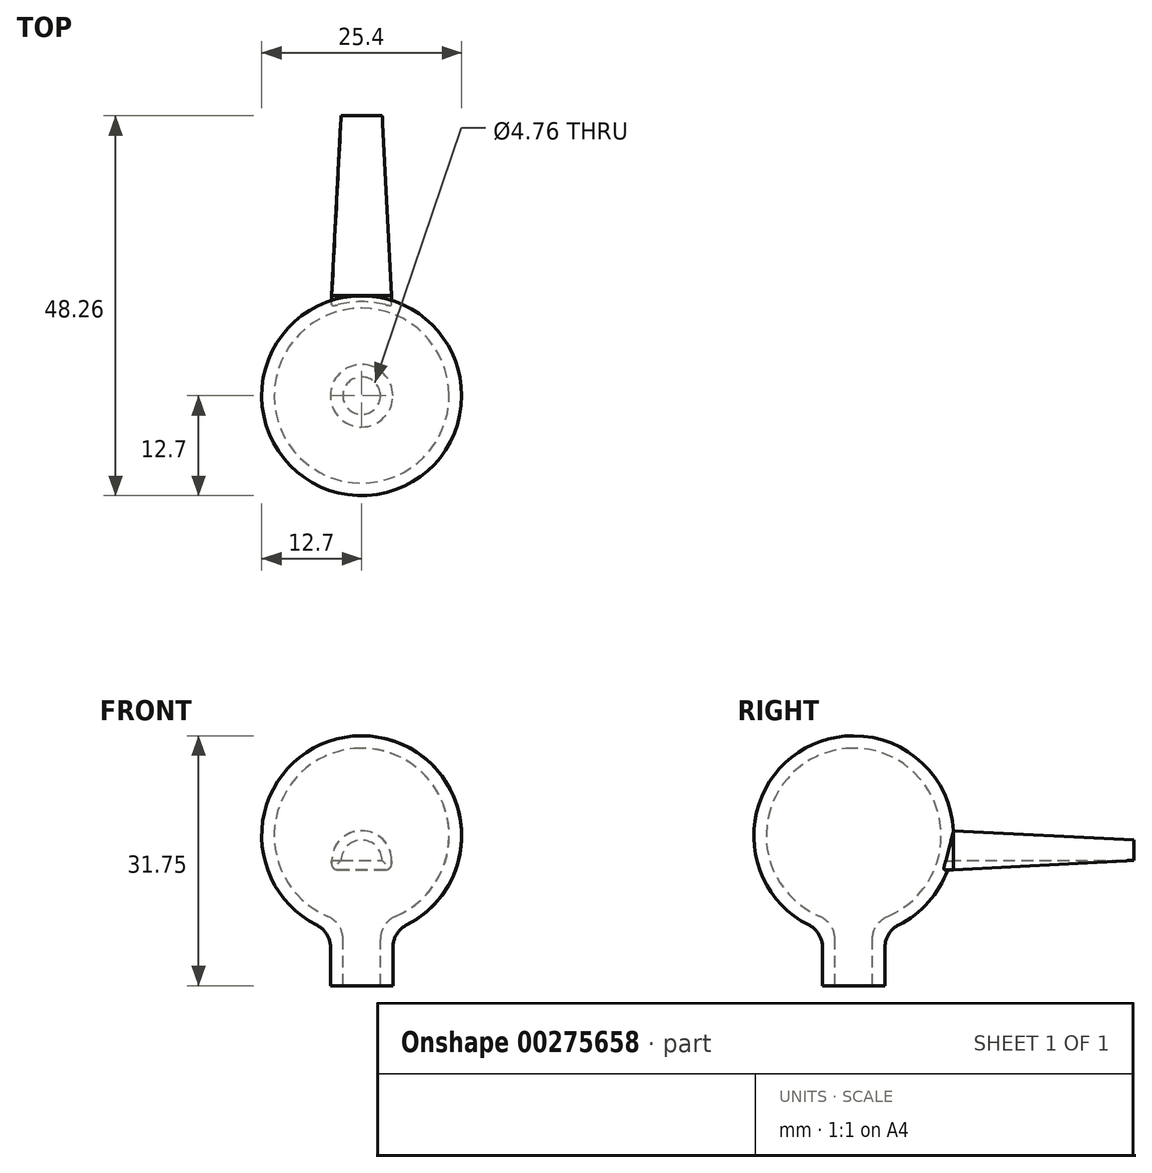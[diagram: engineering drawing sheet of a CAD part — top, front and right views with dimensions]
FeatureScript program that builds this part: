
annotation { "Feature Type Name" : "Feature", "Feature Type Description" : "" }
export const myFeature = defineFeature(function(context is Context, id is Id, definition is map)
    precondition{}
    {
        {
            var Q0;
            Q0=qCreatedBy(makeId("Front.planeOp"),FACE);
            var sketch = newSketch(context, id + "F0", { "sketchPlane" : qUnion([Q0])});
            skLineSegment(sketch, "E0", {"start": v(0, 34.18) * mm, "end": v(0, -34) * mm, "construction": true});
            skLineSegment(sketch, "E1", {"start": v(-21.94, 19.05) * mm, "end": v(23.63, 19.05) * mm, "construction": true});
            skArc(sketch, "E2", {"start": v(5.71, 7.7) * mm, "mid": v(12.36, 21.99) * mm, "end": v(0, 31.75) * mm});
            skArc(sketch, "E3", {"start": v(4.32, 8.81) * mm, "mid": v(10.9, 21.25) * mm, "end": v(0, 30.16) * mm});
            skLineSegment(sketch, "E4", {"start": v(3.97, 0) * mm, "end": v(3.97, 4.87) * mm});
            skLineSegment(sketch, "E5", {"start": v(2.38, 5.89) * mm, "end": v(2.38, 0) * mm});
            skPoint(sketch, "E6.visualSharp", {"position": v(3.97, 6.99) * mm});
            skArc(sketch, "E6.filletArc", {"start": v(5.71, 7.7) * mm, "mid": v(4.44, 6.54) * mm, "end": v(3.97, 4.87) * mm});
            skPoint(sketch, "E7.visualSharp", {"position": v(2.38, 8.2) * mm});
            skArc(sketch, "E7.filletArc", {"start": v(4.32, 8.81) * mm, "mid": v(2.91, 7.64) * mm, "end": v(2.38, 5.89) * mm});
            skLineSegment(sketch, "E8", {"start": v(0, 31.75) * mm, "end": v(0, 30.16) * mm});
            skLineSegment(sketch, "E9", {"start": v(2.38, 0) * mm, "end": v(3.97, 0) * mm});
            skLineSegment(sketch, "E10", {"start": v(-21.69, 15.87) * mm, "end": v(23.57, 15.87) * mm, "construction": true});
            skSolve(sketch);
        }
        {
            var Q0;
            Q0=makeQuery(id+"F0.imprint","IMPRINT",FACE,{"disambiguationData":[TD([[makeQuery(id+"F0.imprint","IMPRINT",EDGE,{"derivedFrom":sQuery(id+"F0.wireOp",EDGE,"E2")}),1.0]])]});
            var Q1;
            Q1=sQuery(id+"F0.wireOp",EDGE,"E0");
            revolve(context, id + "F1", {"entities" : qUnion([Q0]), "axis" : qUnion([Q1]), "revolveType" : RevolveType.FULL});
        }
        {
            var Q0;
            Q0=qCreatedBy(makeId("Front.planeOp"),FACE);
            cPlane(context, id + "F2", {"entities" : qUnion([Q0]), "cplaneType" : CPlaneType.OFFSET, "offset" : 12.7 * mm, "oppositeDirection" : true, "width" : 152.4 * mm, "height" : 152.4 * mm});
        }
        {
            var Q0;
            Q0=qCreatedBy(id+"F2.planeOp",FACE);
            var sketch = newSketch(context, id + "F3", { "sketchPlane" : qUnion([Q0])});
            skLineSegment(sketch, "E11", {"start": v(18.33, 15.88) * mm, "end": v(-19.87, 15.87) * mm, "construction": true});
            skArc(sketch, "E12", {"start": v(3.81, 15.87) * mm, "mid": v(0, 19.68) * mm, "end": v(-3.81, 15.87) * mm});
            skLineSegment(sketch, "E13", {"start": v(3.81, 15.87) * mm, "end": v(3.81, 15.5) * mm});
            skLineSegment(sketch, "E14", {"start": v(3.05, 14.73) * mm, "end": v(-3.06, 14.73) * mm});
            skLineSegment(sketch, "E15", {"start": v(-3.82, 15.51) * mm, "end": v(-3.81, 15.87) * mm});
            skPoint(sketch, "E16.visualSharp", {"position": v(3.81, 14.73) * mm});
            skArc(sketch, "E16.filletArc", {"start": v(3.05, 14.73) * mm, "mid": v(3.59, 14.95) * mm, "end": v(3.8, 15.5) * mm});
            skPoint(sketch, "E17.visualSharp", {"position": v(-3.84, 14.73) * mm});
            skArc(sketch, "E17.filletArc", {"start": v(-3.82, 15.51) * mm, "mid": v(-3.6, 14.96) * mm, "end": v(-3.06, 14.73) * mm});
            skSolve(sketch);
        }
        {
            var Q0;
            Q0=makeQuery(id+"F3.imprint","IMPRINT",FACE,{"disambiguationData":[TD([[makeQuery(id+"F3.imprint","IMPRINT",EDGE,{"derivedFrom":sQuery(id+"F3.wireOp",EDGE,"E12")}),1.0]])]});
            var Q1;
            Q1=makeQuery(id+"F1.opRevolve","SWEPT_FACE",FACE,{"disambiguationData":[OSD([sQuery(id+"F0.wireOp",EDGE,"E2")])]});
            extrude(context, id + "F4", {"entities" : qUnion([Q0]), "operationType" : NewBodyOperationType.ADD, "endBound" : BoundingType.UP_TO_SURFACE, "endBoundEntityFace" : qUnion([Q1]), "depth" : 25.4 * mm});
        }
        {
            var Q0;
            Q0=makeQuery(id+"F4.opExtrude","CAP_FACE",FACE,{"disambiguationData":[OSD([sQuery(id+"F3.wireOp",EDGE,"E12"),sQuery(id+"F3.wireOp",EDGE,"E13"),sQuery(id+"F3.wireOp",EDGE,"E14"),sQuery(id+"F3.wireOp",EDGE,"E15"),sQuery(id+"F3.wireOp",EDGE,"E16.filletArc"),sQuery(id+"F3.wireOp",EDGE,"E17.filletArc")])],"isStart":true});
            extrude(context, id + "F5", {"entities" : qUnion([Q0]), "operationType" : NewBodyOperationType.ADD, "depth" : 22.86 * mm, "hasDraft" : true, "draftAngle" : 3 * degree, "draftPullDirection" : true});
        }
    });
